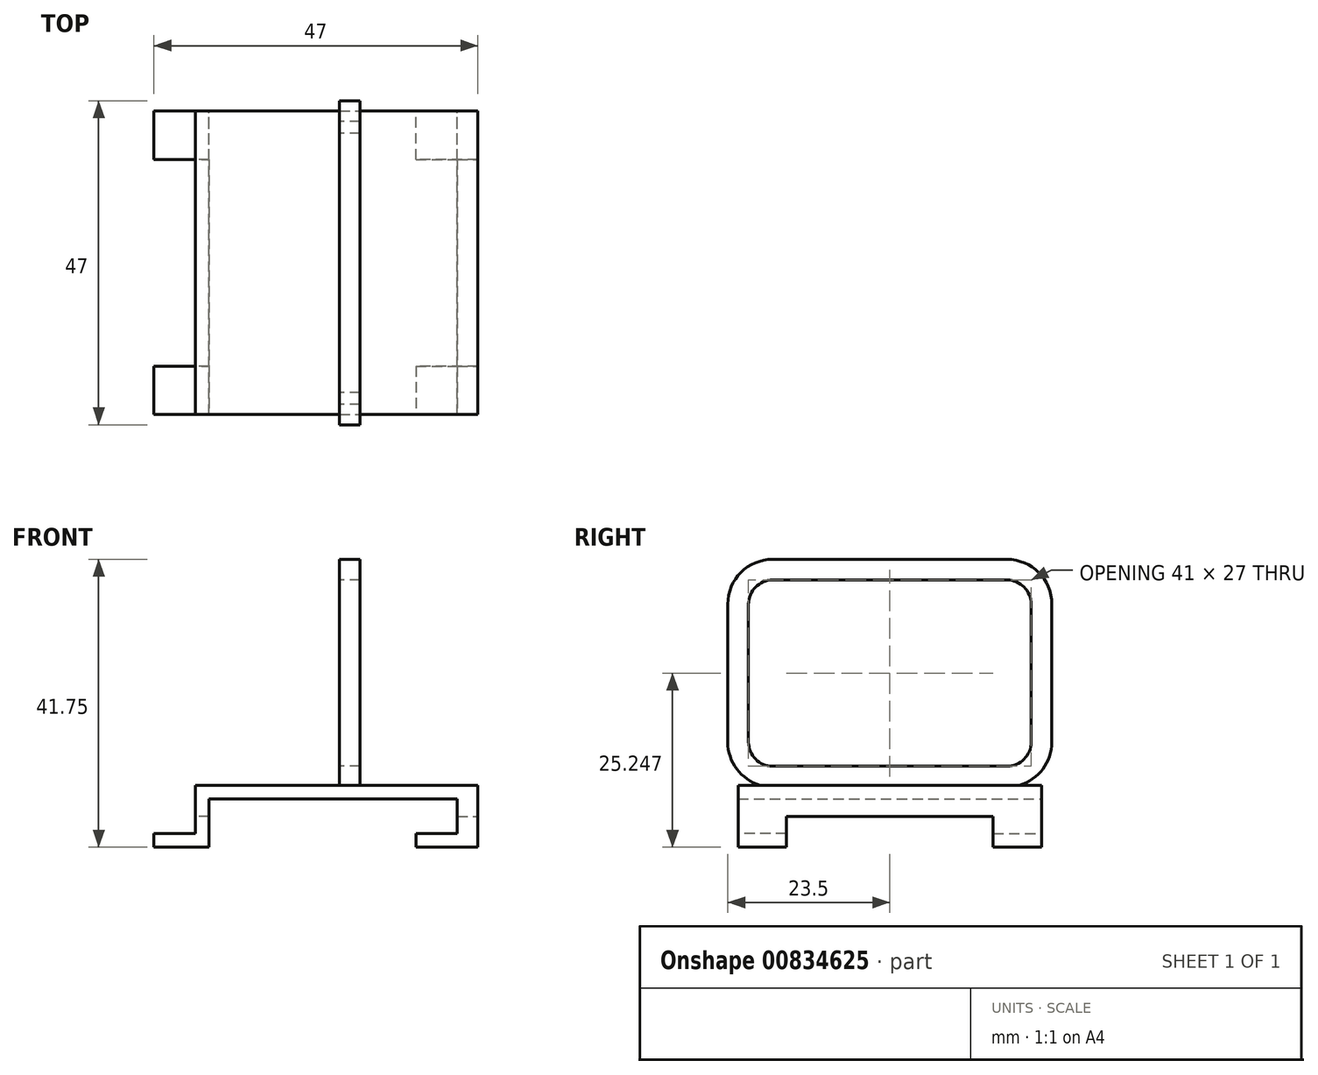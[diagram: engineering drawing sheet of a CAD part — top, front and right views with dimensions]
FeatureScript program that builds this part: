
annotation { "Feature Type Name" : "Feature", "Feature Type Description" : "" }
export const myFeature = defineFeature(function(context is Context, id is Id, definition is map)
    precondition{}
    {
        {
            var Q0;
            Q0=qCreatedBy(makeId("Front.planeOp"),FACE);
            var sketch = newSketch(context, id + "F0", { "sketchPlane" : qUnion([Q0])});
            skLineSegment(sketch, "E0", {"start": v(-28.4, 0) * mm, "end": v(-22.4, 0) * mm});
            skLineSegment(sketch, "E1", {"start": v(-22.4, 0) * mm, "end": v(-22.4, 7) * mm});
            skLineSegment(sketch, "E2", {"start": v(-22.4, 7) * mm, "end": v(18.6, 7) * mm});
            skLineSegment(sketch, "E3.0", {"start": v(-20.4, 5) * mm, "end": v(13.6, 5) * mm});
            skLineSegment(sketch, "E3.1", {"start": v(-20.4, -2) * mm, "end": v(-20.4, 5) * mm});
            skLineSegment(sketch, "E3.2", {"start": v(-28.4, -2) * mm, "end": v(-20.4, -2) * mm});
            skLineSegment(sketch, "E4", {"start": v(18.6, 7) * mm, "end": v(18.6, -2) * mm});
            skLineSegment(sketch, "E5", {"start": v(18.6, -2) * mm, "end": v(9.6, -2) * mm});
            skLineSegment(sketch, "E6", {"start": v(9.6, -2) * mm, "end": v(9.6, 0) * mm});
            skLineSegment(sketch, "E7", {"start": v(9.6, 0) * mm, "end": v(15.6, 0) * mm});
            skLineSegment(sketch, "E8", {"start": v(15.6, 0) * mm, "end": v(15.6, 5) * mm});
            skLineSegment(sketch, "E9", {"start": v(15.6, 5) * mm, "end": v(13.6, 5) * mm});
            skLineSegment(sketch, "E10", {"start": v(-28.4, -2) * mm, "end": v(-28.4, 0) * mm});
            skSolve(sketch);
        }
        {
            var Q0;
            Q0=makeQuery(id+"F0.imprint","IMPRINT",FACE,{"disambiguationData":[TD([[makeQuery(id+"F0.imprint","IMPRINT",EDGE,{"derivedFrom":sQuery(id+"F0.wireOp",EDGE,"E0")}),-1.0]])]});
            extrude(context, id + "F1", {"entities" : qUnion([Q0]), "depth" : 22 * mm, "offsetDistance" : 25 * mm});
        }
        {
            var Q0;
            Q0=makeQuery(id+"F1.opExtrude","CAP_FACE",FACE,{"disambiguationData":[OSD([sQuery(id+"F0.wireOp",EDGE,"E0"),sQuery(id+"F0.wireOp",EDGE,"E1"),sQuery(id+"F0.wireOp",EDGE,"E2"),sQuery(id+"F0.wireOp",EDGE,"E3.0"),sQuery(id+"F0.wireOp",EDGE,"E3.1"),sQuery(id+"F0.wireOp",EDGE,"E3.2"),sQuery(id+"F0.wireOp",EDGE,"E4"),sQuery(id+"F0.wireOp",EDGE,"E5"),sQuery(id+"F0.wireOp",EDGE,"E6"),sQuery(id+"F0.wireOp",EDGE,"E7"),sQuery(id+"F0.wireOp",EDGE,"E8"),sQuery(id+"F0.wireOp",EDGE,"E9"),sQuery(id+"F0.wireOp",EDGE,"E10")])],"isStart":false});
            var sketch = newSketch(context, id + "F2", { "sketchPlane" : qUnion([Q0])});
            skLineSegment(sketch, "E11", {"start": v(-22.4, 0) * mm, "end": v(-20.4, 0) * mm});
            skLineSegment(sketch, "E12", {"start": v(15.6, 0) * mm, "end": v(18.6, 0) * mm});
            skLineSegment(sketch, "E13", {"start": v(15.6, 2.5) * mm, "end": v(18.6, 2.5) * mm});
            skLineSegment(sketch, "E14", {"start": v(-20.4, 2.5) * mm, "end": v(-22.4, 2.5) * mm});
            skSolve(sketch);
        }
        {
            var Q0;
            Q0=qCreatedBy(makeId("Right.planeOp"),FACE);
            var sketch = newSketch(context, id + "F3", { "sketchPlane" : qUnion([Q0])});
            skLineSegment(sketch, "E15", {"start": v(-5, 8.25) * mm, "end": v(-22.25, 8.25) * mm});
            skLineSegment(sketch, "E16", {"start": v(0, 13.25) * mm, "end": v(0, 33.25) * mm});
            skLineSegment(sketch, "E17", {"start": v(-5, 38.25) * mm, "end": v(-22.25, 38.25) * mm});
            skPoint(sketch, "E18.visualSharp", {"position": v(0, 8.25) * mm});
            skArc(sketch, "E18.filletArc", {"start": v(-5, 8.25) * mm, "mid": v(-1.46, 9.71) * mm, "end": v(0, 13.25) * mm});
            skPoint(sketch, "E19.visualSharp", {"position": v(0, 38.25) * mm});
            skArc(sketch, "E19.filletArc", {"start": v(0, 33.25) * mm, "mid": v(-1.46, 36.78) * mm, "end": v(-5, 38.25) * mm});
            skSolve(sketch);
        }
        {
            var Q0;
            Q0 = qSketchRegion(id + "F2", true);
            var Q1;
            {var subQ0=sQuery(id+"F2.wireOp",EDGE,"E11");Q1=makeQuery(id+"F2.imprint","IMPRINT",FACE,{"disambiguationData":[TD([[makeQuery(id+"F2.imprint","IMPRINT",EDGE,{"derivedFrom":subQ0}),-1.0]])]});}
            var Q2;
            {var subQ1=sQuery(id+"F2.wireOp",EDGE,"E12");Q2=makeQuery(id+"F2.imprint","IMPRINT",FACE,{"disambiguationData":[TD([[makeQuery(id+"F2.imprint","IMPRINT",EDGE,{"derivedFrom":subQ1}),-1.0]])]});}
            var Q3;
            {var subQ0=sQuery(id+"F2.wireOp",EDGE,"E11");Q3=makeQuery(id+"F2.imprint","IMPRINT",FACE,{"disambiguationData":[TD([[makeQuery(id+"F2.imprint","IMPRINT",EDGE,{"derivedFrom":subQ0}),1.0]])]});}
            var Q4;
            {var subQ0=sQuery(id+"F2.wireOp",EDGE,"E12");Q4=makeQuery(id+"F2.imprint","IMPRINT",FACE,{"disambiguationData":[TD([[makeQuery(id+"F2.imprint","IMPRINT",EDGE,{"derivedFrom":subQ0}),1.0]])]});}
            extrude(context, id + "F4", {"entities" : qUnion([Q0, Q1, Q2, Q3, Q4]), "operationType" : NewBodyOperationType.REMOVE, "oppositeDirection" : true, "depth" : 15 * mm, "offsetDistance" : 25 * mm});
        }
        {
            var Q0;
            {var subQ3=sQuery(id+"F2.wireOp",EDGE,"E13");Q0=makeQuery(id+"F2.imprint","IMPRINT",FACE,{"disambiguationData":[TD([[makeQuery(id+"F2.imprint","IMPRINT",EDGE,{"derivedFrom":subQ3}),1.0]])]});}
            cPlane(context, id + "F5", {"entities" : qUnion([Q0]), "cplaneType" : CPlaneType.OFFSET, "offset" : 0 * mm, "width" : 150 * mm, "height" : 150 * mm});
        }
        {
            var Q0;
            Q0=qCreatedBy(id+"F5.planeOp",FACE);
            var sketch = newSketch(context, id + "F6", { "sketchPlane" : qUnion([Q0])});
            skLineSegment(sketch, "E20.bottom", {"start": v(1.5, 6.75) * mm, "end": v(-1.5, 6.75) * mm});
            skLineSegment(sketch, "E20.top", {"start": v(1.5, 9.75) * mm, "end": v(-1.5, 9.75) * mm});
            skLineSegment(sketch, "E20.left", {"start": v(1.5, 6.75) * mm, "end": v(1.5, 9.75) * mm});
            skLineSegment(sketch, "E20.right", {"start": v(-1.5, 6.75) * mm, "end": v(-1.5, 9.75) * mm});
            skPoint(sketch, "E20.middle", {"position": v(0, 8.25) * mm});
            skSolve(sketch);
        }
        {
            var Q0;
            Q0=makeQuery(id+"F6.imprint","IMPRINT",FACE,{"disambiguationData":[TD([[makeQuery(id+"F6.imprint","IMPRINT",EDGE,{"derivedFrom":sQuery(id+"F6.wireOp",EDGE,"E20.bottom")}),-1.0]])]});
            var Q1;
            Q1=sQuery(id+"F3.wireOp",EDGE,"E15");
            var Q2;
            Q2=sQuery(id+"F3.wireOp",EDGE,"E18.filletArc");
            var Q3;
            Q3=sQuery(id+"F3.wireOp",EDGE,"E19.filletArc");
            var Q4;
            Q4=sQuery(id+"F3.wireOp",EDGE,"E17");
            var Q5;
            Q5=sQuery(id+"F3.wireOp",EDGE,"E16");
            sweep(context, id + "F7", {"operationType" : NewBodyOperationType.ADD, "profiles" : qUnion([Q0]), "path" : qUnion([Q1, Q2, Q3, Q4, Q5])});
        }
        {
            var Q0;
            Q0=makeQuery(id+"F1.opExtrude","SWEPT_BODY",BODY,{"disambiguationData":[OSD([sQuery(id+"F0.wireOp",EDGE,"E0"),sQuery(id+"F0.wireOp",EDGE,"E1"),sQuery(id+"F0.wireOp",EDGE,"E2"),sQuery(id+"F0.wireOp",EDGE,"E3.0"),sQuery(id+"F0.wireOp",EDGE,"E3.1"),sQuery(id+"F0.wireOp",EDGE,"E3.2"),sQuery(id+"F0.wireOp",EDGE,"E4"),sQuery(id+"F0.wireOp",EDGE,"E5"),sQuery(id+"F0.wireOp",EDGE,"E6"),sQuery(id+"F0.wireOp",EDGE,"E7"),sQuery(id+"F0.wireOp",EDGE,"E8"),sQuery(id+"F0.wireOp",EDGE,"E9"),sQuery(id+"F0.wireOp",EDGE,"E10")])]});
            var Q1;
            Q1=qCreatedBy(id+"F5.planeOp",FACE);
            mirror(context, id + "F8", {"operationType" : NewBodyOperationType.ADD, "entities" : qUnion([Q0]), "mirrorPlane" : qUnion([Q1])});
        }
    });
